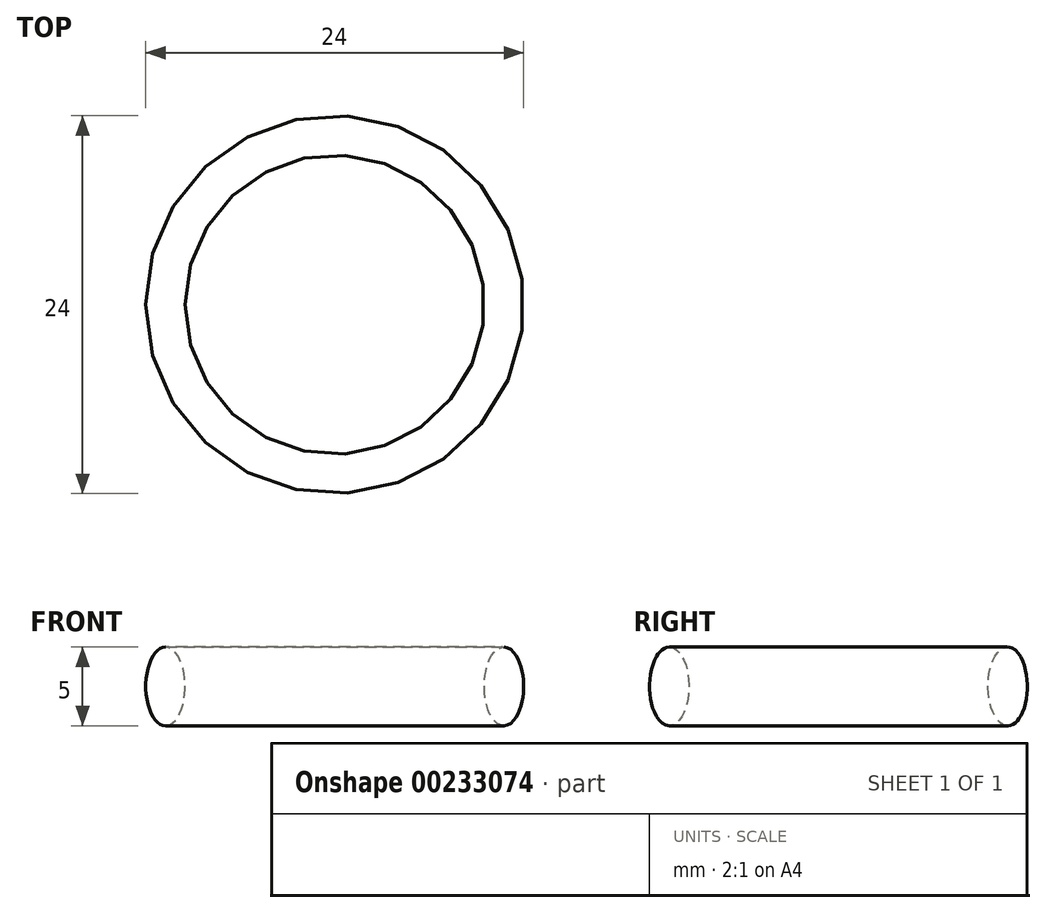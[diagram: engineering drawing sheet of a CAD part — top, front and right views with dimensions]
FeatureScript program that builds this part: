
annotation { "Feature Type Name" : "Feature", "Feature Type Description" : "" }
export const myFeature = defineFeature(function(context is Context, id is Id, definition is map)
    precondition{}
    {
        {
            var Q0;
            Q0=qCreatedBy(makeId("Front.planeOp"),FACE);
            var sketch = newSketch(context, id + "F0", { "sketchPlane" : qUnion([Q0])});
            skEllipse(sketch, "E0", {"center": v(-10.75, 0) * mm, "majorRadius": 2.5 * mm, "minorRadius": 1.25 * mm, "majorAxis": v(0, 1)});
            skLineSegment(sketch, "E1", {"start": v(0, 6.2) * mm, "end": v(0, -7.67) * mm, "construction": true});
            skSolve(sketch);
        }
        {
            var Q0;
            Q0 = qSketchRegion(id + "F0", true);
            var Q1;
            Q1=sQuery(id+"F0.wireOp",EDGE,"E1");
            revolve(context, id + "F1", {"entities" : qUnion([Q0]), "axis" : qUnion([Q1]), "revolveType" : RevolveType.FULL});
        }
    });
